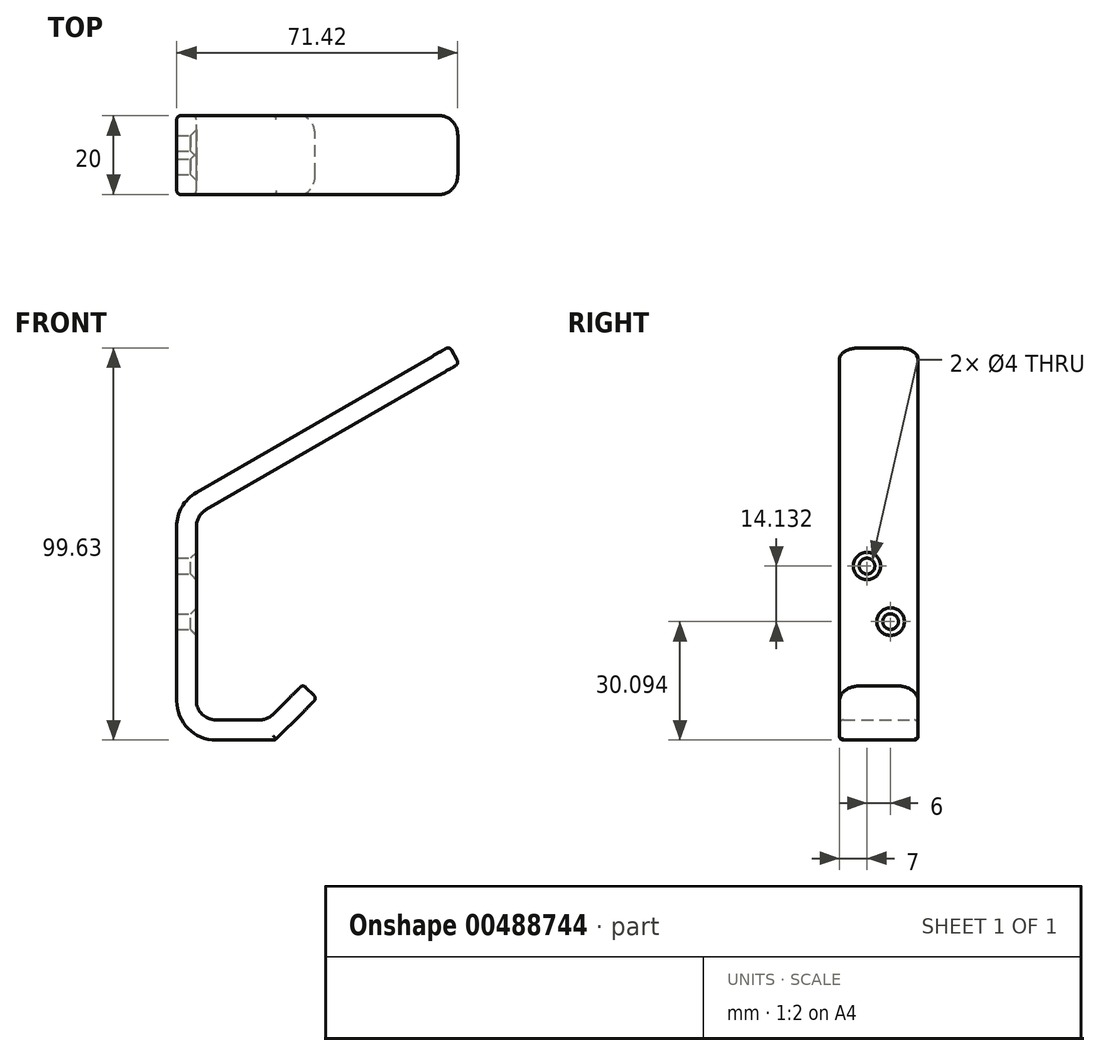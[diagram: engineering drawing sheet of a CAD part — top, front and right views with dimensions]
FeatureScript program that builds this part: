
annotation { "Feature Type Name" : "Feature", "Feature Type Description" : "" }
export const myFeature = defineFeature(function(context is Context, id is Id, definition is map)
    precondition{}
    {
        {
            var Q0;
            Q0=qCreatedBy(makeId("Front.planeOp"),FACE);
            var sketch = newSketch(context, id + "F0", { "sketchPlane" : qUnion([Q0])});
            skLineSegment(sketch, "E0", {"start": v(-27.16, 13.6) * mm, "end": v(-27.16, -46.4) * mm});
            skLineSegment(sketch, "E1", {"start": v(-27.16, 13.6) * mm, "end": v(42.13, 53.6) * mm});
            skLineSegment(sketch, "E2", {"start": v(-2.16, -46.4) * mm, "end": v(8.45, -35.78) * mm});
            skLineSegment(sketch, "E3", {"start": v(8.45, -35.78) * mm, "end": v(4.92, -32.25) * mm});
            skLineSegment(sketch, "E4", {"start": v(42.13, 53.6) * mm, "end": v(44.63, 49.28) * mm});
            skLineSegment(sketch, "E5", {"start": v(44.63, 49.28) * mm, "end": v(-22.16, 10.72) * mm});
            skLineSegment(sketch, "E6", {"start": v(-22.16, -41.3) * mm, "end": v(-22.16, 10.72) * mm});
            skLineSegment(sketch, "E7", {"start": v(-22.16, -41.3) * mm, "end": v(-4.13, -41.3) * mm});
            skLineSegment(sketch, "E8", {"start": v(-27.16, -46.4) * mm, "end": v(-2.16, -46.4) * mm});
            skLineSegment(sketch, "E9", {"start": v(-4.13, -41.3) * mm, "end": v(4.92, -32.25) * mm});
            skLineSegment(sketch, "E10", {"start": v(-19.41, 34.05) * mm, "end": v(22.76, 60.9) * mm});
            skLineSegment(sketch, "E11", {"start": v(-23.85, 39.37) * mm, "end": v(40.04, 80.53) * mm});
            skSolve(sketch);
        }
        {
            var Q0;
            Q0 = qSketchRegion(id + "F0", true);
            extrude(context, id + "F1", {"entities" : qUnion([Q0]), "depth" : 20 * mm});
        }
        {
            var Q0;
            Q0=makeQuery(id+"F1.opExtrude","SWEPT_EDGE",EDGE,{"disambiguationData":[OSD([sQuery(id+"F0.wireOp",EDGE,"E6"),sQuery(id+"F0.wireOp",EDGE,"E7")])]});
            fillet(context, id + "F2", {"entities" : qUnion([Q0]), "radius" : 5 * mm, "tangentPropagation" : true, "allowEdgeOverflow" : false});
        }
        {
            var Q0;
            Q0=makeQuery(id+"F1.opExtrude","SWEPT_EDGE",EDGE,{"disambiguationData":[OSD([sQuery(id+"F0.wireOp",EDGE,"E7"),sQuery(id+"F0.wireOp",EDGE,"E9")])]});
            fillet(context, id + "F3", {"entities" : qUnion([Q0]), "radius" : 5 * mm, "tangentPropagation" : true, "allowEdgeOverflow" : false});
        }
        {
            var Q0;
            Q0=makeQuery(id+"F1.opExtrude","SWEPT_EDGE",EDGE,{"disambiguationData":[OSD([sQuery(id+"F0.wireOp",EDGE,"E0"),sQuery(id+"F0.wireOp",EDGE,"E8")])]});
            var Q1;
            Q1=makeQuery(id+"F1.opExtrude","SWEPT_EDGE",EDGE,{"disambiguationData":[OSD([sQuery(id+"F0.wireOp",EDGE,"E0"),sQuery(id+"F0.wireOp",EDGE,"E1")])]});
            fillet(context, id + "F4", {"entities" : qUnion([Q0, Q1]), "radius" : 10 * mm, "tangentPropagation" : true, "allowEdgeOverflow" : false});
        }
        {
            var Q0;
            Q0=makeQuery(id+"F1.opExtrude","SWEPT_EDGE",EDGE,{"disambiguationData":[OSD([sQuery(id+"F0.wireOp",EDGE,"E5"),sQuery(id+"F0.wireOp",EDGE,"E6")])]});
            fillet(context, id + "F5", {"entities" : qUnion([Q0]), "radius" : 5 * mm, "tangentPropagation" : true, "allowEdgeOverflow" : false});
        }
        {
            var Q0;
            Q0=makeQuery(id+"F1.opExtrude","CAP_EDGE",EDGE,{"disambiguationData":[OSD([sQuery(id+"F0.wireOp",EDGE,"E3")])],"isStart":true});
            fillet(context, id + "F6", {"entities" : qUnion([Q0]), "radius" : 5 * mm, "tangentPropagation" : true, "allowEdgeOverflow" : false});
        }
        {
            var Q0;
            Q0=makeQuery(id+"F1.opExtrude","CAP_EDGE",EDGE,{"disambiguationData":[OSD([sQuery(id+"F0.wireOp",EDGE,"E3")])],"isStart":false});
            fillet(context, id + "F7", {"entities" : qUnion([Q0]), "radius" : 5 * mm, "tangentPropagation" : true, "allowEdgeOverflow" : false});
        }
        {
            var Q0;
            Q0=makeQuery(id+"F1.opExtrude","CAP_EDGE",EDGE,{"disambiguationData":[OSD([sQuery(id+"F0.wireOp",EDGE,"E4")])],"isStart":false});
            fillet(context, id + "F8", {"entities" : qUnion([Q0]), "radius" : 5 * mm, "tangentPropagation" : true, "allowEdgeOverflow" : false});
        }
        {
            var Q0;
            Q0=makeQuery(id+"F1.opExtrude","CAP_EDGE",EDGE,{"disambiguationData":[OSD([sQuery(id+"F0.wireOp",EDGE,"E4")])],"isStart":true});
            fillet(context, id + "F9", {"entities" : qUnion([Q0]), "radius" : 5 * mm, "tangentPropagation" : true, "allowEdgeOverflow" : false});
        }
        {
            var Q0;
            Q0=makeQuery(id+"F8.opFillet","BLEND_EDGE",EDGE,{"blendedFrom":[makeQuery(id+"F1.opExtrude","CAP_EDGE",EDGE,{"disambiguationData":[OSD([sQuery(id+"F0.wireOp",EDGE,"E4")])],"isStart":false}),makeQuery(id+"F1.opExtrude","SWEPT_FACE",FACE,{"disambiguationData":[OSD([sQuery(id+"F0.wireOp",EDGE,"E5")])]})],"blendedInto":[makeQuery(id+"F1.opExtrude","SWEPT_FACE",FACE,{"disambiguationData":[OSD([sQuery(id+"F0.wireOp",EDGE,"E5")])]})]});
            fillet(context, id + "F10", {"entities" : qUnion([Q0]), "radius" : 1 * mm, "tangentPropagation" : true, "allowEdgeOverflow" : false});
        }
        {
            var Q0;
            Q0=makeQuery(id+"F7.opFillet","BLEND_EDGE",EDGE,{"blendedFrom":[makeQuery(id+"F1.opExtrude","CAP_EDGE",EDGE,{"disambiguationData":[OSD([sQuery(id+"F0.wireOp",EDGE,"E3")])],"isStart":false}),makeQuery(id+"F1.opExtrude","SWEPT_FACE",FACE,{"disambiguationData":[OSD([sQuery(id+"F0.wireOp",EDGE,"E2")])]})],"blendedInto":[makeQuery(id+"F1.opExtrude","SWEPT_FACE",FACE,{"disambiguationData":[OSD([sQuery(id+"F0.wireOp",EDGE,"E2")])]})]});
            fillet(context, id + "F11", {"entities" : qUnion([Q0]), "radius" : 1 * mm, "tangentPropagation" : true, "allowEdgeOverflow" : false});
        }
        {
            var Q0;
            {var subQ0=sQuery(id+"F0.wireOp",EDGE,"E8");var subQ1=sQuery(id+"F0.wireOp",EDGE,"E0");Q0=makeQuery(id+"F4.opFillet","BLEND_EDGE",EDGE,{"blendedFrom":[makeQuery(id+"F1.opExtrude","SWEPT_EDGE",EDGE,{"disambiguationData":[OSD([subQ1,subQ0])]}),makeQuery(id+"F1.opExtrude","CAP_FACE",FACE,{"disambiguationData":[OSD([subQ1,sQuery(id+"F0.wireOp",EDGE,"E1"),sQuery(id+"F0.wireOp",EDGE,"E2"),sQuery(id+"F0.wireOp",EDGE,"E3"),sQuery(id+"F0.wireOp",EDGE,"E4"),sQuery(id+"F0.wireOp",EDGE,"E5"),sQuery(id+"F0.wireOp",EDGE,"E6"),sQuery(id+"F0.wireOp",EDGE,"E7"),subQ0,sQuery(id+"F0.wireOp",EDGE,"E9")])],"isStart":false})],"blendedInto":[makeQuery(id+"F1.opExtrude","CAP_FACE",FACE,{"disambiguationData":[OSD([subQ1,sQuery(id+"F0.wireOp",EDGE,"E1"),sQuery(id+"F0.wireOp",EDGE,"E2"),sQuery(id+"F0.wireOp",EDGE,"E3"),sQuery(id+"F0.wireOp",EDGE,"E4"),sQuery(id+"F0.wireOp",EDGE,"E5"),sQuery(id+"F0.wireOp",EDGE,"E6"),sQuery(id+"F0.wireOp",EDGE,"E7"),subQ0,sQuery(id+"F0.wireOp",EDGE,"E9")])],"isStart":false})]});}
            fillet(context, id + "F12", {"entities" : qUnion([Q0]), "radius" : 1 * mm, "tangentPropagation" : true, "allowEdgeOverflow" : false});
        }
        {
            var Q0;
            Q0=makeQuery(id+"F1.opExtrude","SWEPT_FACE",FACE,{"disambiguationData":[OSD([sQuery(id+"F0.wireOp",EDGE,"E6")])]});
            var sketch = newSketch(context, id + "F13", { "sketchPlane" : qUnion([Q0])});
            skPoint(sketch, "E12", {"position": v(-13, -2.16) * mm});
            skPoint(sketch, "E13", {"position": v(-7, -16.3) * mm});
            skSolve(sketch);
        }
        {
            var Q0;
            Q0=sQuery(id+"F13.wireOp",VERTEX,"E12");
            var Q1;
            Q1=makeQuery(id+"F1.opExtrude","SWEPT_BODY",BODY,{"disambiguationData":[OSD([sQuery(id+"F0.wireOp",EDGE,"E0"),sQuery(id+"F0.wireOp",EDGE,"E1"),sQuery(id+"F0.wireOp",EDGE,"E2"),sQuery(id+"F0.wireOp",EDGE,"E3"),sQuery(id+"F0.wireOp",EDGE,"E4"),sQuery(id+"F0.wireOp",EDGE,"E5"),sQuery(id+"F0.wireOp",EDGE,"E6"),sQuery(id+"F0.wireOp",EDGE,"E7"),sQuery(id+"F0.wireOp",EDGE,"E8"),sQuery(id+"F0.wireOp",EDGE,"E9")])]});
            hole(context, id + "F14", {"style" : HoleStyle.C_SINK, "endStyle" : HoleEndStyle.THROUGH, "holeDiameter" : 4 * mm, "cSinkDiameter" : 7 * mm, "cSinkAngle" : 90 * degree, "isTappedThrough" : true, "tappedDepth" : 12 * mm, "tapClearance" : 3, "locations" : qUnion([Q0]), "scope" : qUnion([Q1])});
        }
        {
            var Q0;
            Q0=sQuery(id+"F13.wireOp",VERTEX,"E13");
            var Q1;
            Q1=makeQuery(id+"F1.opExtrude","SWEPT_BODY",BODY,{"disambiguationData":[OSD([sQuery(id+"F0.wireOp",EDGE,"E0"),sQuery(id+"F0.wireOp",EDGE,"E1"),sQuery(id+"F0.wireOp",EDGE,"E2"),sQuery(id+"F0.wireOp",EDGE,"E3"),sQuery(id+"F0.wireOp",EDGE,"E4"),sQuery(id+"F0.wireOp",EDGE,"E5"),sQuery(id+"F0.wireOp",EDGE,"E6"),sQuery(id+"F0.wireOp",EDGE,"E7"),sQuery(id+"F0.wireOp",EDGE,"E8"),sQuery(id+"F0.wireOp",EDGE,"E9")])]});
            hole(context, id + "F15", {"style" : HoleStyle.C_SINK, "endStyle" : HoleEndStyle.THROUGH, "holeDiameter" : 4 * mm, "cSinkDiameter" : 7 * mm, "cSinkAngle" : 90 * degree, "isTappedThrough" : true, "tappedDepth" : 12 * mm, "tapClearance" : 3, "locations" : qUnion([Q0]), "scope" : qUnion([Q1])});
        }
    });
